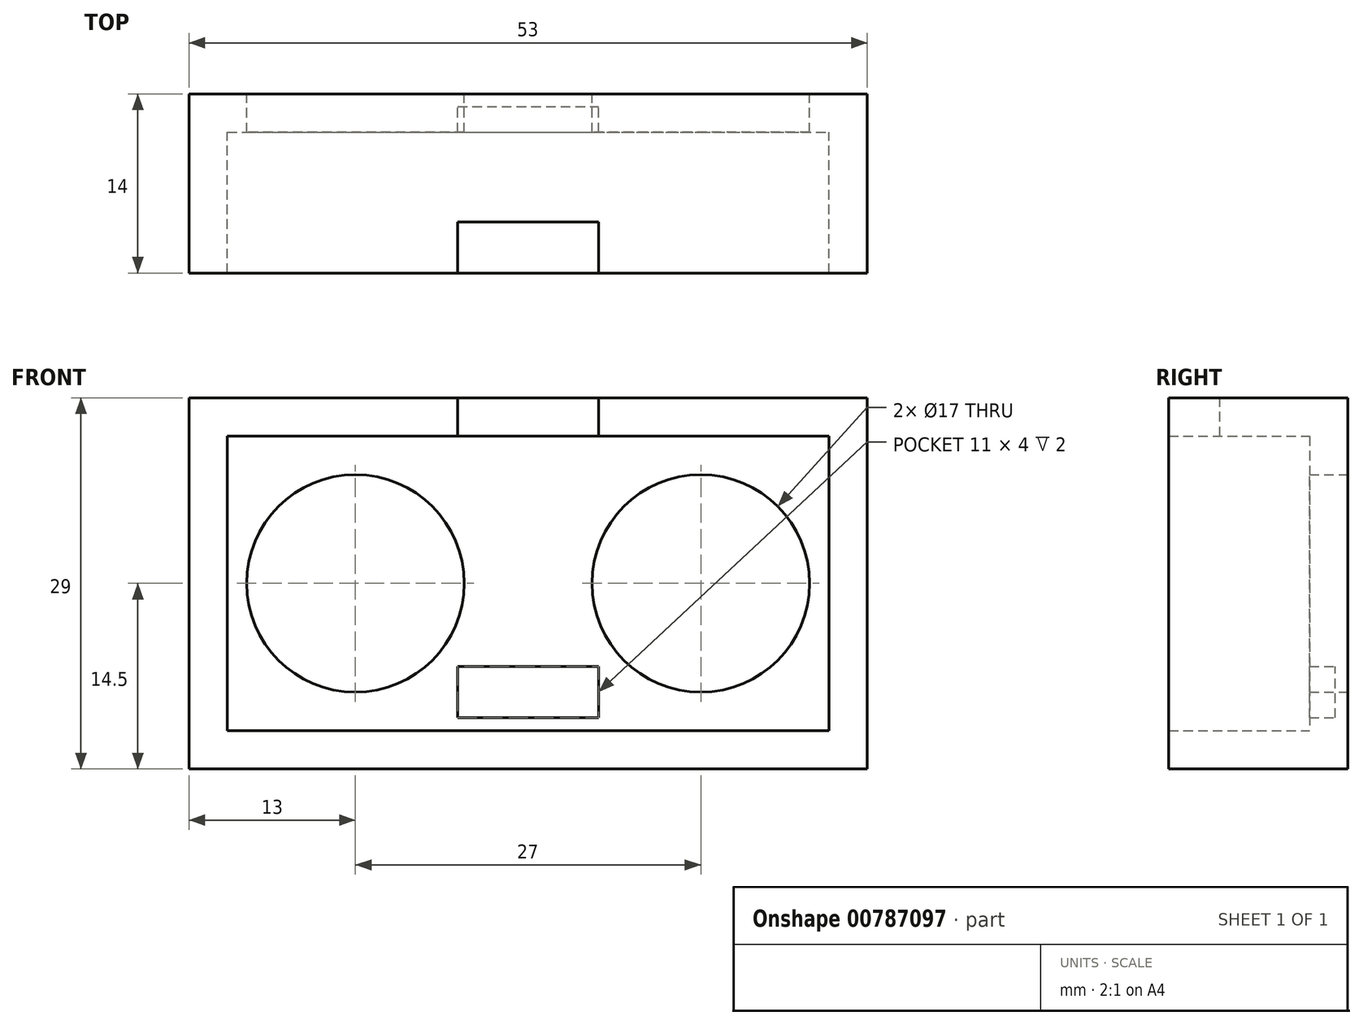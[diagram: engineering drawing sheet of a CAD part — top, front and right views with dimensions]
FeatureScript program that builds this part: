
annotation { "Feature Type Name" : "Feature", "Feature Type Description" : "" }
export const myFeature = defineFeature(function(context is Context, id is Id, definition is map)
    precondition{}
    {
        {
            var Q0;
            Q0=qCreatedBy(makeId("Front.planeOp"),FACE);
            var sketch = newSketch(context, id + "F0", { "sketchPlane" : qUnion([Q0])});
            skLineSegment(sketch, "E0.bottom", {"start": v(-23.5, 11.5) * mm, "end": v(23.5, 11.5) * mm});
            skLineSegment(sketch, "E0.top", {"start": v(-23.5, -11.5) * mm, "end": v(23.5, -11.5) * mm});
            skLineSegment(sketch, "E0.left", {"start": v(-23.5, 11.5) * mm, "end": v(-23.5, -11.5) * mm});
            skLineSegment(sketch, "E0.right", {"start": v(23.5, 11.5) * mm, "end": v(23.5, -11.5) * mm});
            skPoint(sketch, "E0.middle", {"position": v(0, 0) * mm});
            skPoint(sketch, "E1", {"position": v(-13.5, 0) * mm});
            skCircle(sketch, "E2", {"center": v(-13.5, 0) * mm, "radius": 8.5 * mm});
            skCircle(sketch, "E3.MirrorC", {"center": v(13.5, 0) * mm, "radius": 8.5 * mm});
            skPoint(sketch, "E4", {"position": v(0, -8.5) * mm});
            skPoint(sketch, "E4.positionSnap0", {"position": v(0, -11.5) * mm});
            skLineSegment(sketch, "E5.bottom", {"start": v(-5.5, -10.5) * mm, "end": v(5.5, -10.5) * mm});
            skLineSegment(sketch, "E5.top", {"start": v(-5.5, -6.5) * mm, "end": v(5.5, -6.5) * mm});
            skLineSegment(sketch, "E5.left", {"start": v(-5.5, -10.5) * mm, "end": v(-5.5, -6.5) * mm});
            skLineSegment(sketch, "E5.right", {"start": v(5.5, -10.5) * mm, "end": v(5.5, -6.5) * mm});
            skLineSegment(sketch, "E6.bottom", {"start": v(-23.5, 11.5) * mm, "end": v(-26.5, 11.5) * mm});
            skLineSegment(sketch, "E6.top", {"start": v(-23.5, -11.5) * mm, "end": v(-26.5, -11.5) * mm});
            skLineSegment(sketch, "E6.right", {"start": v(-26.5, 11.5) * mm, "end": v(-26.5, -11.5) * mm});
            skLineSegment(sketch, "E7.bottom", {"start": v(23.5, 11.5) * mm, "end": v(26.5, 11.5) * mm});
            skLineSegment(sketch, "E7.top", {"start": v(23.5, -11.5) * mm, "end": v(26.5, -11.5) * mm});
            skLineSegment(sketch, "E7.right", {"start": v(26.5, 11.5) * mm, "end": v(26.5, -11.5) * mm});
            skLineSegment(sketch, "E8.bottom", {"start": v(-26.5, 11.5) * mm, "end": v(26.5, 11.5) * mm});
            skLineSegment(sketch, "E8.top", {"start": v(-26.5, 14.5) * mm, "end": v(26.5, 14.5) * mm});
            skLineSegment(sketch, "E8.left", {"start": v(-26.5, 11.5) * mm, "end": v(-26.5, 14.5) * mm});
            skLineSegment(sketch, "E8.right", {"start": v(26.5, 11.5) * mm, "end": v(26.5, 14.5) * mm});
            skLineSegment(sketch, "E9.bottom", {"start": v(-26.5, -11.5) * mm, "end": v(26.5, -11.5) * mm});
            skLineSegment(sketch, "E9.top", {"start": v(-26.5, -14.5) * mm, "end": v(26.5, -14.5) * mm});
            skLineSegment(sketch, "E9.left", {"start": v(-26.5, -11.5) * mm, "end": v(-26.5, -14.5) * mm});
            skLineSegment(sketch, "E9.right", {"start": v(26.5, -11.5) * mm, "end": v(26.5, -14.5) * mm});
            skLineSegment(sketch, "E10.bottom", {"start": v(-5.5, -11.5) * mm, "end": v(5.5, -11.5) * mm});
            skLineSegment(sketch, "E10.top", {"start": v(-5.5, -14.5) * mm, "end": v(5.5, -14.5) * mm});
            skLineSegment(sketch, "E10.left", {"start": v(-5.5, -11.5) * mm, "end": v(-5.5, -14.5) * mm});
            skLineSegment(sketch, "E10.right", {"start": v(5.5, -11.5) * mm, "end": v(5.5, -14.5) * mm});
            skLineSegment(sketch, "E11.bottom", {"start": v(-5.5, 11.5) * mm, "end": v(5.5, 11.5) * mm});
            skLineSegment(sketch, "E11.top", {"start": v(-5.5, 14.5) * mm, "end": v(5.5, 14.5) * mm});
            skLineSegment(sketch, "E11.left", {"start": v(-5.5, 11.5) * mm, "end": v(-5.5, 14.5) * mm});
            skLineSegment(sketch, "E11.right", {"start": v(5.5, 11.5) * mm, "end": v(5.5, 14.5) * mm});
            skSolve(sketch);
        }
        {
            var Q0;
            {var subQ1=sQuery(id+"F0.wireOp",EDGE,"E0.left");Q0=makeQuery(id+"F0.imprint","IMPRINT",FACE,{"disambiguationData":[TD([[makeQuery(id+"F0.imprint","IMPRINT",EDGE,{"derivedFrom":subQ1}),1.0]])]});}
            extrude(context, id + "F1", {"entities" : qUnion([Q0]), "depth" : 3 * mm, "offsetDistance" : 25 * mm});
        }
        {
            var Q0;
            Q0=makeQuery(id+"F0.imprint","IMPRINT",FACE,{"disambiguationData":[TD([[makeQuery(id+"F0.imprint","IMPRINT",EDGE,{"derivedFrom":sQuery(id+"F0.wireOp",EDGE,"E5.bottom")}),1.0]])]});
            extrude(context, id + "F2", {"entities" : qUnion([Q0]), "operationType" : NewBodyOperationType.ADD, "depth" : 1 * mm, "offsetDistance" : 25 * mm});
        }
        {
            var Q0;
            {var subQ3=sQuery(id+"F0.wireOp",EDGE,"E7.bottom");var subQ7=sQuery(id+"F0.wireOp",EDGE,"E6.bottom");Q0=qUnion([makeQuery(id+"F0.imprint","IMPRINT",FACE,{"disambiguationData":[TD([[makeQuery(id+"F0.imprint","IMPRINT",EDGE,{"derivedFrom":subQ7}),-1.0]])]}),makeQuery(id+"F0.imprint","IMPRINT",FACE,{"disambiguationData":[TD([[makeQuery(id+"F0.imprint","IMPRINT",EDGE,{"derivedFrom":subQ3}),1.0]])]})]);}
            var Q1;
            Q1=makeQuery(id+"F0.imprint","IMPRINT",FACE,{"disambiguationData":[TD([[makeQuery(id+"F0.imprint","IMPRINT",EDGE,{"derivedFrom":sQuery(id+"F0.wireOp",EDGE,"E0.left")}),-1.0]])]});
            var Q2;
            {var subQ3=sQuery(id+"F0.wireOp",EDGE,"E6.top");var subQ6=sQuery(id+"F0.wireOp",EDGE,"E7.top");Q2=qUnion([makeQuery(id+"F0.imprint","IMPRINT",FACE,{"disambiguationData":[TD([[makeQuery(id+"F0.imprint","IMPRINT",EDGE,{"derivedFrom":subQ6}),-1.0]])]}),makeQuery(id+"F0.imprint","IMPRINT",FACE,{"disambiguationData":[TD([[makeQuery(id+"F0.imprint","IMPRINT",EDGE,{"derivedFrom":subQ3}),1.0]])]})]);}
            var Q3;
            Q3=makeQuery(id+"F0.imprint","IMPRINT",FACE,{"disambiguationData":[TD([[makeQuery(id+"F0.imprint","IMPRINT",EDGE,{"derivedFrom":sQuery(id+"F0.wireOp",EDGE,"E0.right")}),1.0]])]});
            var Q4;
            {var subQ2=sQuery(id+"F0.wireOp",EDGE,"E10.left");Q4=makeQuery(id+"F0.imprint","IMPRINT",FACE,{"disambiguationData":[TD([[makeQuery(id+"F0.imprint","IMPRINT",EDGE,{"derivedFrom":subQ2}),1.0]])]});}
            extrude(context, id + "F3", {"entities" : qUnion([Q0, Q1, Q2, Q3, Q4]), "operationType" : NewBodyOperationType.ADD, "depth" : 14 * mm, "offsetDistance" : 25 * mm});
        }
        {
            var Q0;
            {var subQ2=sQuery(id+"F0.wireOp",EDGE,"E11.left");Q0=makeQuery(id+"F0.imprint","IMPRINT",FACE,{"disambiguationData":[TD([[makeQuery(id+"F0.imprint","IMPRINT",EDGE,{"derivedFrom":subQ2}),-1.0]])]});}
            extrude(context, id + "F4", {"entities" : qUnion([Q0]), "operationType" : NewBodyOperationType.ADD, "depth" : 10 * mm, "offsetDistance" : 25 * mm});
        }
    });
